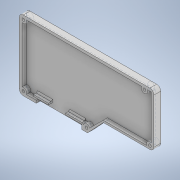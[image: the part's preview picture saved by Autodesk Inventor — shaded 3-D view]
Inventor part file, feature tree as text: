
AUTODESK INVENTOR PART (.ipt)
format: ipt  version: 2021 (Build 250183000, 183)  size: 292,352 bytes
history: native  units: mm
features: sketch x11, extrude x10, fillet x2, hole x1, chamfer x1
ambient origin geometry x8: Origin, YZ Plane, XZ Plane, XY Plane, X Axis, Y Axis, Z Axis, Center Point
bodies: Solid1 (feature_tree)
feature tree (25):
  extrude  "Extrusion1"  Depth=100.0mm
  extrude  "Extrusion2"  Depth=50.0mm
  hole  "Hole1"  [1 undecoded]
  extrude  "Extrusion3"  Depth=50.0mm
  extrude  "Extrusion4"  Depth=3.0mm
  extrude  "Extrusion5"  Depth=3.0mm
  fillet  "Fillet1"  Radius=49.0mm
  extrude  "Extrusion6"  Depth=49.0mm
  extrude  "Extrusion7"  Depth=5.0mm
  extrude  "Extrusion8"  Depth=5.0mm
  chamfer  "Chamfer1"  Distance=2.0mm
  extrude  "Extrusion9"  Depth=5.0mm
  fillet  "Fillet2"  Radius=2.0mm
  extrude  "Extrusion11"  Depth=5.0mm
  sketch  "Sketch1"  dims[d0=52.0mm d1=100.0mm]
  sketch  "Sketch2"  dims[d2=26.0mm d3=50.0mm]
  sketch  "Sketch3"  dims[d4=2.0mm d5=0.0mm d6=3.0mm]
  sketch  "Sketch4"  dims[d7=3.0mm d8=50.0mm]
  sketch  "Sketch5"  dims[d9=3.0mm d10=97.0mm]
  sketch  "Sketch6"  dims[d11=15.0mm d12=3.0mm d13=49.0mm]
  sketch  "Sketch7"  dims[d14=93.0mm d15=49.0mm]
  sketch  "Sketch8"  dims[d16=2.0mm d17=5.0mm]
  sketch  "Sketch9"  dims[d18=2.0mm d19=5.0mm]
  sketch  "Sketch10"  dims[d20=2.0mm]
  sketch  "Sketch12"  dims[d21=5.0mm d22=2.0mm d23=5.0mm d24=2.0mm d25=5.0mm d26=3.0mm d27=0.0mm d28=2.0mm d29=6.0mm d30=5.0mm d31=2.0mm d32=90.0deg d33=10.0mm d34=20.594885mm d35=12.5mm d36=62.35mm d37=3.0mm d38=0.0mm d39=50.673mm d40=3.0mm d41=0.0mm d42=2.0mm d43=2.0mm d44=2.0mm d45=1.5mm d46=3.0mm d47=0.0mm d48=3.0mm d49=7.6mm d50=46.4mm d51=6.7mm d52=3.0mm d53=0.0mm d54=5.0mm d55=2.0mm d56=12.0mm d57=0.0mm d58=1.4mm d59=1.2mm d60=3.0mm d61=14.0mm d62=1.2mm d63=1.4mm d64=12.0mm d65=3.0mm d66=0.0mm d67=1.0mm d68=2.0mm d69=45.0deg d70=1.2mm d71=3.0mm d72=0.0mm d73=1.0mm d77=3.0mm d78=0.0mm d74=0.872665mm d75=0.872665mm d76=0.5mm]
note: 1 required parameter value undecoded (feature->parameter linkage not recoverable at this tier; creation-order binding heuristic only, values carry confidence <= 0.55)
